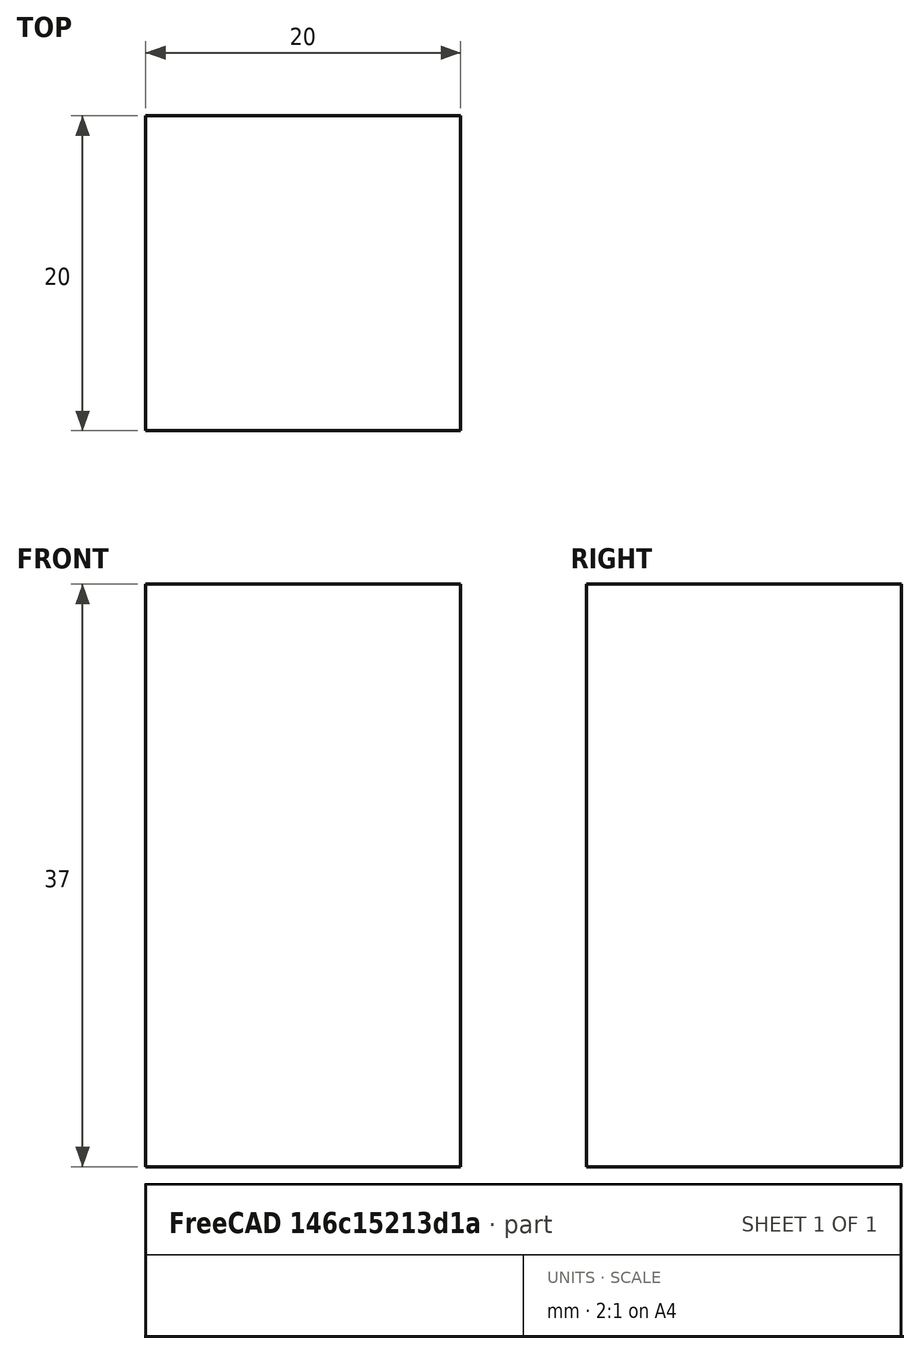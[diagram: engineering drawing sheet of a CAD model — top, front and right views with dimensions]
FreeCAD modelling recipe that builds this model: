
FCSTD DOCUMENT  (FreeCAD 0.19R24276 (Git))
Label: L37
License: All rights reserved
LicenseURL: http://en.wikipedia.org/wiki/All_rights_reserved
objects: Sketcher::SketchObject×1, PartDesign::Pad×1, PartDesign::Body×1
note: 4 computed .brp shape members not serialized (recipe doc carries the construction recipe); baked Part::Feature solids carry a one-line shape summary decoded from their .brp

FEATURE [Sketcher::SketchObject] Sketch
  FullyConstrained = true
  MapMode = 5
  Support = -> [XY_Plane]
  sketch-geometry (4):
    g0: LineSegment StartX=0 StartY=0 StartZ=0 EndX=20 EndY=0 EndZ=0
    g1: LineSegment StartX=20 StartY=0 StartZ=0 EndX=20 EndY=-20 EndZ=0
    g2: LineSegment StartX=20 StartY=-20 StartZ=0 EndX=0 EndY=-20 EndZ=0
    g3: LineSegment StartX=0 StartY=-20 StartZ=0 EndX=0 EndY=0 EndZ=0
  constraints (11):
    c: Coincident(g0,g1)
    c: Coincident(g1,g2)
    c: Coincident(g2,g3)
    c: Coincident(g3,g0)
    c: Horizontal(g0)
    c: Horizontal(g2)
    c: Vertical(g1)
    c: Vertical(g3)
    c: Coincident(g0,g-1)
    c: Equal(g2,g1)
    c: DistanceY(g1,g1) = 20
FEATURE [PartDesign::Pad] Pad
  Direction = (1,1,1)
  Length = 37
  Length2 = 100
  Profile = -> Sketch
  Type = 0
FEATURE [PartDesign::Body] Body
  Group = -> [Sketch,Pad]
  Origin = -> Origin
  Tip = -> Pad
